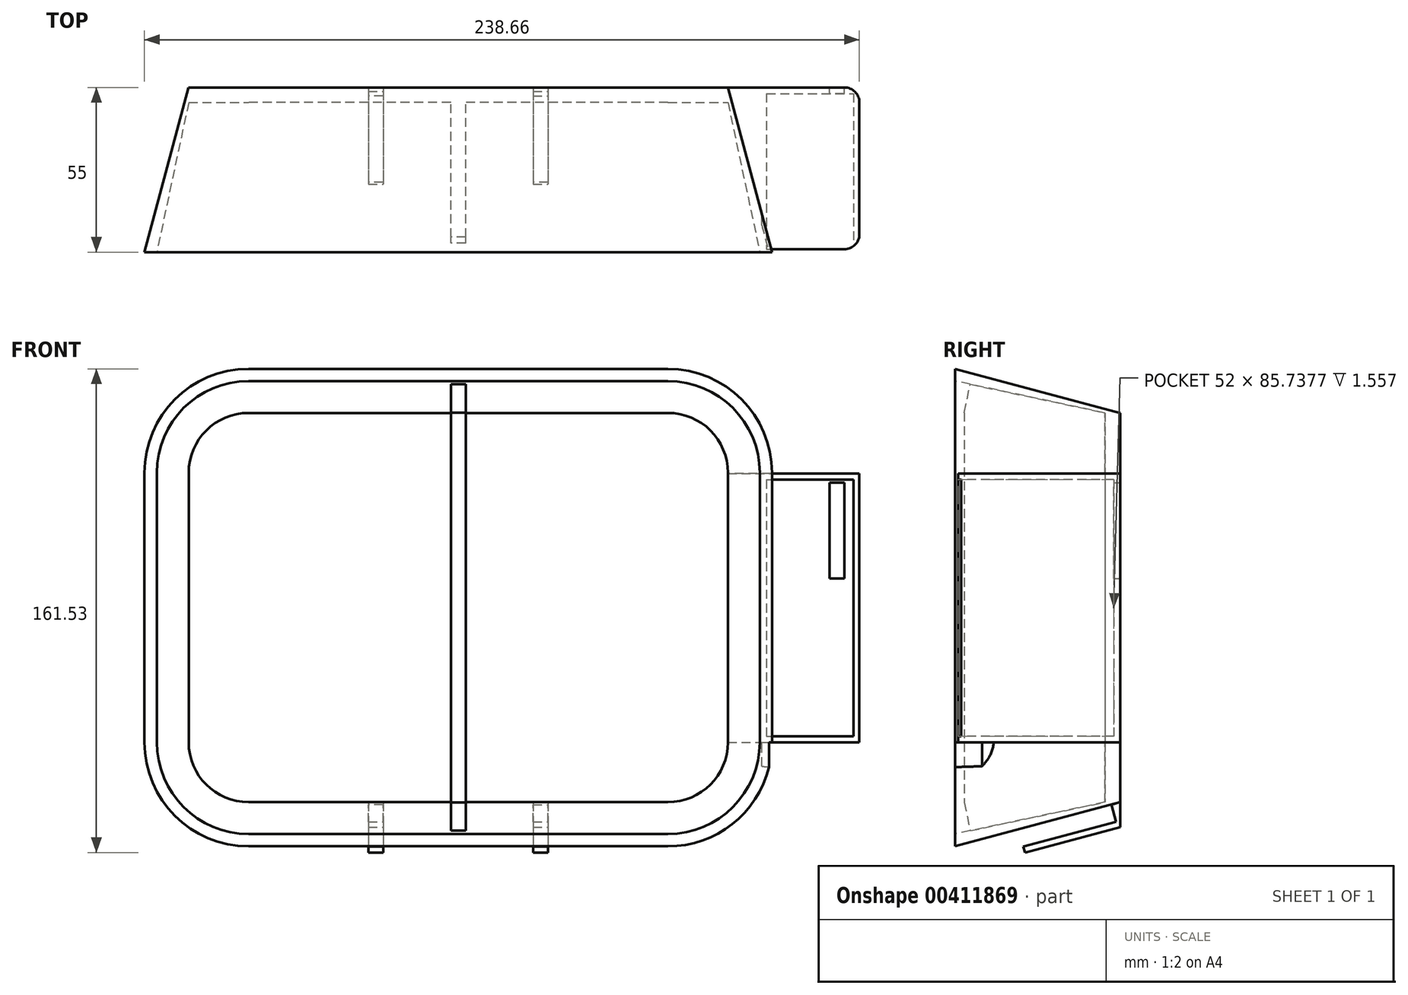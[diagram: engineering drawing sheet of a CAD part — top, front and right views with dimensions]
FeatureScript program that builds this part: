
annotation { "Feature Type Name" : "Feature", "Feature Type Description" : "" }
export const myFeature = defineFeature(function(context is Context, id is Id, definition is map)
    precondition{}
    {
        {
            var Q0;
            Q0=qCreatedBy(makeId("Front.planeOp"),FACE);
            var sketch = newSketch(context, id + "F0", { "sketchPlane" : qUnion([Q0])});
            skLineSegment(sketch, "E0.bottom", {"start": v(-105.92, 85.19) * mm, "end": v(34.08, 85.19) * mm});
            skLineSegment(sketch, "E0.top", {"start": v(-105.92, -44.81) * mm, "end": v(34.08, -44.81) * mm});
            skLineSegment(sketch, "E0.left", {"start": v(-125.92, 65.19) * mm, "end": v(-125.92, -24.81) * mm});
            skLineSegment(sketch, "E0.right", {"start": v(54.08, 65.19) * mm, "end": v(54.08, -24.81) * mm});
            skPoint(sketch, "E1.visualSharp", {"position": v(54.08, 85.19) * mm});
            skArc(sketch, "E1.filletArc", {"start": v(54.08, 65.19) * mm, "mid": v(48.22, 79.33) * mm, "end": v(34.08, 85.19) * mm});
            skArc(sketch, "E2.filletArc", {"start": v(34.08, -44.81) * mm, "mid": v(48.22, -38.95) * mm, "end": v(54.08, -24.81) * mm});
            skArc(sketch, "E3.filletArc", {"start": v(-125.92, -24.81) * mm, "mid": v(-120.06, -38.95) * mm, "end": v(-105.92, -44.81) * mm});
            skPoint(sketch, "E4.visualSharp", {"position": v(-125.92, 85.19) * mm});
            skArc(sketch, "E4.filletArc", {"start": v(-105.92, 85.19) * mm, "mid": v(-120.06, 79.33) * mm, "end": v(-125.92, 65.19) * mm});
            skSolve(sketch);
        }
        {
            var Q0;
            Q0=makeQuery(id+"F0.imprint","IMPRINT",FACE,{"disambiguationData":[TD([[makeQuery(id+"F0.imprint","IMPRINT",EDGE,{"derivedFrom":sQuery(id+"F0.wireOp",EDGE,"E0.bottom")}),-1.0]])]});
            extrude(context, id + "F1", {"entities" : qUnion([Q0]), "depth" : 55 * mm, "hasDraft" : true, "draftAngle" : 15 * degree});
        }
        {
            var Q0;
            Q0=makeQuery(id+"F1.opExtrude","CAP_FACE",FACE,{"disambiguationData":[OSD([sQuery(id+"F0.wireOp",EDGE,"E0.bottom"),sQuery(id+"F0.wireOp",EDGE,"E0.top"),sQuery(id+"F0.wireOp",EDGE,"E0.left"),sQuery(id+"F0.wireOp",EDGE,"E0.right"),sQuery(id+"F0.wireOp",EDGE,"E1.filletArc"),sQuery(id+"F0.wireOp",EDGE,"E2.filletArc"),sQuery(id+"F0.wireOp",EDGE,"E3.filletArc"),sQuery(id+"F0.wireOp",EDGE,"E4.filletArc")])],"isStart":false});
            cPlane(context, id + "F2", {"entities" : qUnion([Q0]), "cplaneType" : CPlaneType.OFFSET, "offset" : 50 * mm, "oppositeDirection" : true, "width" : 150 * mm, "height" : 150 * mm});
        }
        {
            var Q0;
            Q0=qCreatedBy(id+"F2.planeOp",FACE);
            var sketch = newSketch(context, id + "F3", { "sketchPlane" : qUnion([Q0])});
            skLineSegment(sketch, "E5.bottom", {"start": v(-105.9, 85.22) * mm, "end": v(34.1, 85.22) * mm});
            skLineSegment(sketch, "E5.top", {"start": v(-105.9, -44.78) * mm, "end": v(34.1, -44.78) * mm});
            skLineSegment(sketch, "E5.left", {"start": v(-125.9, 65.22) * mm, "end": v(-125.9, -24.78) * mm});
            skLineSegment(sketch, "E5.right", {"start": v(54.1, 65.22) * mm, "end": v(54.1, -24.78) * mm});
            skPoint(sketch, "E6.visualSharp", {"position": v(-125.9, 85.22) * mm});
            skArc(sketch, "E6.filletArc", {"start": v(-105.9, 85.22) * mm, "mid": v(-120.04, 79.36) * mm, "end": v(-125.9, 65.22) * mm});
            skPoint(sketch, "E7.visualSharp", {"position": v(-125.9, -44.78) * mm});
            skArc(sketch, "E7.filletArc", {"start": v(-125.9, -24.78) * mm, "mid": v(-120.04, -38.92) * mm, "end": v(-105.9, -44.78) * mm});
            skPoint(sketch, "E8.visualSharp", {"position": v(54.1, -44.78) * mm});
            skArc(sketch, "E8.filletArc", {"start": v(34.1, -44.78) * mm, "mid": v(48.25, -38.92) * mm, "end": v(54.1, -24.78) * mm});
            skPoint(sketch, "E9.visualSharp", {"position": v(54.1, 85.22) * mm});
            skArc(sketch, "E9.filletArc", {"start": v(54.1, 65.22) * mm, "mid": v(48.25, 79.36) * mm, "end": v(34.1, 85.22) * mm});
            skSolve(sketch);
        }
        {
            var Q0;
            Q0 = qSketchRegion(id + "F3", true);
            extrude(context, id + "F4", {"entities" : qUnion([Q0]), "operationType" : NewBodyOperationType.REMOVE, "depth" : 55 * mm, "hasDraft" : true, "draftAngle" : 12 * degree});
        }
        {
            var Q0;
            Q0=makeQuery(id+"F4.boolean.opBoolean","COPY",FACE,{"derivedFrom":makeQuery(id+"F4.opExtrude","CAP_FACE",FACE,{"disambiguationData":[OSD([sQuery(id+"F3.wireOp",EDGE,"E5.bottom"),sQuery(id+"F3.wireOp",EDGE,"E5.top"),sQuery(id+"F3.wireOp",EDGE,"E5.left"),sQuery(id+"F3.wireOp",EDGE,"E5.right"),sQuery(id+"F3.wireOp",EDGE,"E6.filletArc"),sQuery(id+"F3.wireOp",EDGE,"E7.filletArc"),sQuery(id+"F3.wireOp",EDGE,"E8.filletArc"),sQuery(id+"F3.wireOp",EDGE,"E9.filletArc")])],"isStart":true})});
            var sketch = newSketch(context, id + "F5", { "sketchPlane" : qUnion([Q0])});
            skLineSegment(sketch, "E10.bottom", {"start": v(-38.4, 85.22) * mm, "end": v(-33.4, 85.22) * mm});
            skLineSegment(sketch, "E10.top", {"start": v(-38.4, -64.78) * mm, "end": v(-33.4, -64.78) * mm});
            skLineSegment(sketch, "E10.left", {"start": v(-38.4, 85.22) * mm, "end": v(-38.4, -64.78) * mm});
            skLineSegment(sketch, "E10.right", {"start": v(-33.4, 85.22) * mm, "end": v(-33.4, -64.78) * mm});
            skSolve(sketch);
        }
        {
            var Q0;
            Q0=makeQuery(id+"F5.imprint","IMPRINT",FACE,{"disambiguationData":[TD([[makeQuery(id+"F5.imprint","IMPRINT",EDGE,{"derivedFrom":sQuery(id+"F5.wireOp",EDGE,"E10.bottom")}),-1.0]])]});
            extrude(context, id + "F6", {"entities" : qUnion([Q0]), "operationType" : NewBodyOperationType.ADD, "depth" : 47 * mm});
        }
        {
            var Q0;
            Q0=qCreatedBy(makeId("Right.planeOp"),FACE);
            cPlane(context, id + "F7", {"entities" : qUnion([Q0]), "cplaneType" : CPlaneType.OFFSET, "offset" : 98 * mm, "width" : 150 * mm, "height" : 150 * mm});
        }
        {
            var Q0;
            Q0=qCreatedBy(id+"F7.planeOp",FACE);
            var sketch = newSketch(context, id + "F8", { "sketchPlane" : qUnion([Q0])});
            skLineSegment(sketch, "E11.bottom", {"start": v(-54.03, 64.93) * mm, "end": v(0, 64.93) * mm});
            skLineSegment(sketch, "E11.top", {"start": v(-54.03, -25.17) * mm, "end": v(0, -25.17) * mm});
            skLineSegment(sketch, "E11.left", {"start": v(-54.03, 64.93) * mm, "end": v(-54.03, -25.17) * mm});
            skLineSegment(sketch, "E11.right", {"start": v(0, 64.93) * mm, "end": v(0, -25.17) * mm});
            skSolve(sketch);
        }
        {
            var Q0;
            Q0=makeQuery(id+"F1.opExtrude","SWEPT_FACE",FACE,{"disambiguationData":[OSD([sQuery(id+"F0.wireOp",EDGE,"E0.right")])]});
            var sketch = newSketch(context, id + "F9", { "sketchPlane" : qUnion([Q0])});
            skLineSegment(sketch, "E12.bottom", {"start": v(-69.94, 64.93) * mm, "end": v(-14, 64.93) * mm});
            skLineSegment(sketch, "E12.top", {"start": v(-69.94, -24.81) * mm, "end": v(-14, -24.81) * mm});
            skLineSegment(sketch, "E12.left", {"start": v(-69.94, 64.93) * mm, "end": v(-69.94, -24.81) * mm});
            skLineSegment(sketch, "E12.right", {"start": v(-14, 64.93) * mm, "end": v(-14, -24.81) * mm});
            skSolve(sketch);
        }
        {
            var Q0;
            Q0=qCreatedBy(makeId("Front.planeOp"),FACE);
            var sketch = newSketch(context, id + "F10", { "sketchPlane" : qUnion([Q0])});
            skLineSegment(sketch, "E13.bottom", {"start": v(185.4, 123.91) * mm, "end": v(-174.62, 123.91) * mm});
            skLineSegment(sketch, "E13.top", {"start": v(185.4, -101.96) * mm, "end": v(-174.62, -101.96) * mm});
            skLineSegment(sketch, "E13.left", {"start": v(185.4, 123.91) * mm, "end": v(185.4, -101.96) * mm});
            skLineSegment(sketch, "E13.right", {"start": v(-174.62, 123.91) * mm, "end": v(-174.62, -101.96) * mm});
            skSolve(sketch);
        }
        {
            var Q0;
            Q0 = qSketchRegion(id + "F10", true);
            extrude(context, id + "F11", {"entities" : qUnion([Q0]), "operationType" : NewBodyOperationType.REMOVE, "oppositeDirection" : true, "depth" : 25 * mm});
        }
        {
            var Q0;
            Q0=makeQuery(id+"F4.boolean.opBoolean","COPY",FACE,{"derivedFrom":makeQuery(id+"F4.opExtrude","SWEPT_FACE",FACE,{"disambiguationData":[OSD([sQuery(id+"F3.wireOp",EDGE,"E5.top")])]})});
            var sketch = newSketch(context, id + "F12", { "sketchPlane" : qUnion([Q0])});
            skLineSegment(sketch, "E14.bottom", {"start": v(-33.4, -60.2) * mm, "end": v(-38.4, -60.2) * mm});
            skLineSegment(sketch, "E14.top", {"start": v(-33.4, -14.2) * mm, "end": v(-38.4, -14.2) * mm});
            skLineSegment(sketch, "E14.left", {"start": v(-33.4, -60.2) * mm, "end": v(-33.4, -14.2) * mm});
            skLineSegment(sketch, "E14.right", {"start": v(-38.4, -60.2) * mm, "end": v(-38.4, -14.2) * mm});
            skSolve(sketch);
        }
        {
            var Q0;
            Q0 = qSketchRegion(id + "F12", true);
            extrude(context, id + "F13", {"entities" : qUnion([Q0]), "operationType" : NewBodyOperationType.ADD, "depth" : 15 * mm});
        }
        {
            var Q0;
            Q0=makeQuery(id+"F4.boolean.opBoolean","COPY",FACE,{"derivedFrom":makeQuery(id+"F4.opExtrude","SWEPT_FACE",FACE,{"disambiguationData":[OSD([sQuery(id+"F3.wireOp",EDGE,"E5.bottom")])]})});
            var sketch = newSketch(context, id + "F14", { "sketchPlane" : qUnion([Q0])});
            skLineSegment(sketch, "E15.bottom", {"start": v(-38.4, 68.6) * mm, "end": v(-33.4, 68.6) * mm});
            skLineSegment(sketch, "E15.top", {"start": v(-38.4, 22.6) * mm, "end": v(-33.4, 22.6) * mm});
            skLineSegment(sketch, "E15.left", {"start": v(-38.4, 68.6) * mm, "end": v(-38.4, 22.6) * mm});
            skLineSegment(sketch, "E15.right", {"start": v(-33.4, 68.6) * mm, "end": v(-33.4, 22.6) * mm});
            skSolve(sketch);
        }
        {
            var Q0;
            Q0=makeQuery(id+"F14.imprint","IMPRINT",FACE,{"disambiguationData":[TD([[makeQuery(id+"F14.imprint","IMPRINT",EDGE,{"derivedFrom":sQuery(id+"F14.wireOp",EDGE,"E15.bottom")}),-1.0]])]});
            extrude(context, id + "F15", {"entities" : qUnion([Q0]), "operationType" : NewBodyOperationType.ADD, "depth" : 15 * mm});
        }
        {
            var Q0;
            Q0=makeQuery(id+"F8.imprint","IMPRINT",FACE,{"disambiguationData":[TD([[makeQuery(id+"F8.imprint","IMPRINT",EDGE,{"derivedFrom":sQuery(id+"F8.wireOp",EDGE,"E11.bottom")}),-1.0]])]});
            extrude(context, id + "F16", {"entities" : qUnion([Q0]), "operationType" : NewBodyOperationType.ADD, "oppositeDirection" : true, "depth" : 32.6 * mm});
        }
        {
            var Q0;
            Q0=makeQuery(id+"F9.imprint","IMPRINT",FACE,{"disambiguationData":[TD([[makeQuery(id+"F9.imprint","IMPRINT",EDGE,{"derivedFrom":sQuery(id+"F9.wireOp",EDGE,"E12.bottom")}),-1.0]])]});
            extrude(context, id + "F17", {"entities" : qUnion([Q0]), "operationType" : NewBodyOperationType.ADD, "depth" : 25 * mm});
        }
        {
            var Q0;
            Q0=qCreatedBy(makeId("Front.planeOp"),FACE);
            var sketch = newSketch(context, id + "F18", { "sketchPlane" : qUnion([Q0])});
            skLineSegment(sketch, "E16.bottom", {"start": v(-173.75, 128.8) * mm, "end": v(173.98, 128.8) * mm});
            skLineSegment(sketch, "E16.top", {"start": v(-173.75, -88.43) * mm, "end": v(173.98, -88.43) * mm});
            skLineSegment(sketch, "E16.left", {"start": v(-173.75, 128.8) * mm, "end": v(-173.75, -88.43) * mm});
            skLineSegment(sketch, "E16.right", {"start": v(173.98, 128.8) * mm, "end": v(173.98, -88.43) * mm});
            skSolve(sketch);
        }
        {
            var Q0;
            Q0 = qSketchRegion(id + "F18", true);
            extrude(context, id + "F19", {"entities" : qUnion([Q0]), "operationType" : NewBodyOperationType.REMOVE, "oppositeDirection" : true, "depth" : 25 * mm});
        }
        {
            var Q0;
            Q0=makeQuery(id+"F17.opExtrude","SWEPT_FACE",FACE,{"disambiguationData":[OSD([sQuery(id+"F9.wireOp",EDGE,"E12.top")])]});
            var sketch = newSketch(context, id + "F20", { "sketchPlane" : qUnion([Q0])});
            skLineSegment(sketch, "E17.bottom", {"start": v(65.4, 45.99) * mm, "end": v(99.8, 45.99) * mm});
            skLineSegment(sketch, "E17.top", {"start": v(65.4, 0) * mm, "end": v(99.8, 0) * mm});
            skLineSegment(sketch, "E17.left", {"start": v(65.4, 45.99) * mm, "end": v(65.4, 0) * mm});
            skLineSegment(sketch, "E17.right", {"start": v(99.8, 45.99) * mm, "end": v(99.8, 0) * mm});
            skPoint(sketch, "E18.end.orphan", {"position": v(97.92, 45.99) * mm});
            skLineSegment(sketch, "E19", {"start": v(65.4, 45.99) * mm, "end": v(68.02, 55.75) * mm});
            skLineSegment(sketch, "E20", {"start": v(68.02, 55.75) * mm, "end": v(100.28, 55.75) * mm});
            skLineSegment(sketch, "E21", {"start": v(100.28, 55.75) * mm, "end": v(99.8, 45.99) * mm});
            skSolve(sketch);
        }
        {
            var Q0;
            Q0 = qSketchRegion(id + "F20", true);
            extrude(context, id + "F21", {"entities" : qUnion([Q0]), "operationType" : NewBodyOperationType.REMOVE, "depth" : 25 * mm});
        }
        {
            var Q0;
            {var subQ0=sQuery(id+"F8.wireOp",EDGE,"E11.left");var subQ1=sQuery(id+"F8.wireOp",EDGE,"E11.bottom");var subQ3=makeQuery(id+"F16.opExtrude","SWEPT_FACE",FACE,{"disambiguationData":[OSD([subQ0])]});Q0=makeQuery(id+"F21.boolean.opBoolean","SPLIT",FACE,{"disambiguationData":[TD([makeQuery(id+"F16.opExtrude","SWEPT_FACE",FACE,{"disambiguationData":[OSD([subQ1])]})])],"derivedFrom":subQ3});}
            var sketch = newSketch(context, id + "F22", { "sketchPlane" : qUnion([Q0])});
            skLineSegment(sketch, "E22.bottom", {"start": v(67, 62.93) * mm, "end": v(96, 62.93) * mm});
            skLineSegment(sketch, "E22.top", {"start": v(67, -22.81) * mm, "end": v(96, -22.81) * mm});
            skLineSegment(sketch, "E22.left", {"start": v(67, 62.93) * mm, "end": v(67, -22.81) * mm});
            skLineSegment(sketch, "E22.right", {"start": v(96, 62.93) * mm, "end": v(96, -22.81) * mm});
            skSolve(sketch);
        }
        {
            var Q0;
            Q0=makeQuery(id+"F22.imprint","IMPRINT",FACE,{"disambiguationData":[TD([[makeQuery(id+"F22.imprint","IMPRINT",EDGE,{"derivedFrom":sQuery(id+"F22.wireOp",EDGE,"E22.bottom")}),-1.0]])]});
            extrude(context, id + "F23", {"entities" : qUnion([Q0]), "operationType" : NewBodyOperationType.REMOVE, "oppositeDirection" : true, "depth" : 52 * mm});
        }
        {
            var Q0;
            Q0=makeQuery(id+"F16.opExtrude","CAP_EDGE",EDGE,{"disambiguationData":[OSD([sQuery(id+"F8.wireOp",EDGE,"E11.left")])],"isStart":true});
            var Q1;
            Q1=makeQuery(id+"F16.opExtrude","CAP_EDGE",EDGE,{"disambiguationData":[OSD([sQuery(id+"F8.wireOp",EDGE,"E11.right")])],"isStart":true});
            fillet(context, id + "F24", {"entities" : qUnion([Q0, Q1]), "radius" : 5 * mm, "tangentPropagation" : true, "allowEdgeOverflow" : false});
        }
        {
            var Q0;
            Q0=makeQuery(id+"F6.opExtrude","CAP_FACE",FACE,{"disambiguationData":[OSD([sQuery(id+"F3.wireOp",EDGE,"E5.top"),sQuery(id+"F5.wireOp",EDGE,"E10.bottom"),sQuery(id+"F5.wireOp",EDGE,"E10.left"),sQuery(id+"F5.wireOp",EDGE,"E10.right")])],"isStart":false});
            var sketch = newSketch(context, id + "F25", { "sketchPlane" : qUnion([Q0])});
            skLineSegment(sketch, "E23.bottom", {"start": v(-38.4, 92.26) * mm, "end": v(-33.4, 92.26) * mm});
            skLineSegment(sketch, "E23.top", {"start": v(-38.4, -53.07) * mm, "end": v(-33.4, -53.07) * mm});
            skLineSegment(sketch, "E23.left", {"start": v(-38.4, 92.26) * mm, "end": v(-38.4, -56.27) * mm});
            skLineSegment(sketch, "E23.right", {"start": v(-33.4, 92.26) * mm, "end": v(-33.4, -56.27) * mm});
            skSolve(sketch);
        }
        {
            var Q0;
            Q0 = qSketchRegion(id + "F25", true);
            extrude(context, id + "F26", {"entities" : qUnion([Q0]), "operationType" : NewBodyOperationType.REMOVE, "depth" : 25 * mm});
        }
        {
            var Q0;
            Q0=makeQuery(id+"F19.boolean.opBoolean","MERGE",FACE,{"derivedFrom":[makeQuery(id+"F1.opExtrude","CAP_FACE",FACE,{"disambiguationData":[OSD([sQuery(id+"F0.wireOp",EDGE,"E0.bottom"),sQuery(id+"F0.wireOp",EDGE,"E0.top"),sQuery(id+"F0.wireOp",EDGE,"E0.left"),sQuery(id+"F0.wireOp",EDGE,"E0.right"),sQuery(id+"F0.wireOp",EDGE,"E1.filletArc"),sQuery(id+"F0.wireOp",EDGE,"E2.filletArc"),sQuery(id+"F0.wireOp",EDGE,"E3.filletArc"),sQuery(id+"F0.wireOp",EDGE,"E4.filletArc")])],"isStart":true}),makeQuery(id+"F16.opExtrude","SWEPT_FACE",FACE,{"disambiguationData":[OSD([sQuery(id+"F8.wireOp",EDGE,"E11.right")])]}),makeQuery(id+"F19.opExtrude","CAP_FACE",FACE,{"disambiguationData":[OSD([sQuery(id+"F18.wireOp",EDGE,"E16.bottom"),sQuery(id+"F18.wireOp",EDGE,"E16.top"),sQuery(id+"F18.wireOp",EDGE,"E16.left"),sQuery(id+"F18.wireOp",EDGE,"E16.right")])],"isStart":true})]});
            var sketch = newSketch(context, id + "F27", { "sketchPlane" : qUnion([Q0])});
            skLineSegment(sketch, "E24.bottom", {"start": v(-88, 29.93) * mm, "end": v(-93, 29.93) * mm});
            skLineSegment(sketch, "E24.top", {"start": v(-88, 61.93) * mm, "end": v(-93, 61.93) * mm});
            skLineSegment(sketch, "E24.left", {"start": v(-88, 29.93) * mm, "end": v(-88, 61.93) * mm});
            skLineSegment(sketch, "E24.right", {"start": v(-93, 29.93) * mm, "end": v(-93, 61.93) * mm});
            skSolve(sketch);
        }
        {
            var Q0;
            Q0 = qSketchRegion(id + "F27", true);
            extrude(context, id + "F28", {"entities" : qUnion([Q0]), "operationType" : NewBodyOperationType.REMOVE, "oppositeDirection" : true, "depth" : 10 * mm});
        }
        {
            var Q0;
            Q0=makeQuery(id+"F1.opExtrude","SWEPT_FACE",FACE,{"disambiguationData":[OSD([sQuery(id+"F0.wireOp",EDGE,"E0.top")])]});
            var sketch = newSketch(context, id + "F29", { "sketchPlane" : qUnion([Q0])});
            skLineSegment(sketch, "E25.bottom", {"start": v(-60.92, 11.6) * mm, "end": v(-65.92, 11.6) * mm});
            skLineSegment(sketch, "E25.top", {"start": v(-60.92, 46.6) * mm, "end": v(-65.92, 46.6) * mm});
            skLineSegment(sketch, "E25.left", {"start": v(-60.92, 11.6) * mm, "end": v(-60.92, 46.6) * mm});
            skLineSegment(sketch, "E25.right", {"start": v(-65.92, 11.6) * mm, "end": v(-65.92, 46.6) * mm});
            skLineSegment(sketch, "E26.bottom", {"start": v(-5.92, 11.6) * mm, "end": v(-10.92, 11.6) * mm});
            skLineSegment(sketch, "E26.top", {"start": v(-5.92, 46.6) * mm, "end": v(-10.92, 46.6) * mm});
            skLineSegment(sketch, "E26.left", {"start": v(-5.92, 11.6) * mm, "end": v(-5.92, 46.6) * mm});
            skLineSegment(sketch, "E26.right", {"start": v(-10.92, 11.6) * mm, "end": v(-10.92, 46.6) * mm});
            skSolve(sketch);
        }
        {
            var Q0;
            Q0=makeQuery(id+"F29.imprint","IMPRINT",FACE,{"disambiguationData":[TD([[makeQuery(id+"F29.imprint","IMPRINT",EDGE,{"derivedFrom":sQuery(id+"F29.wireOp",EDGE,"E25.bottom")}),1.0]])]});
            var Q1;
            Q1=makeQuery(id+"F29.imprint","IMPRINT",FACE,{"disambiguationData":[TD([[makeQuery(id+"F29.imprint","IMPRINT",EDGE,{"derivedFrom":sQuery(id+"F29.wireOp",EDGE,"E26.bottom")}),1.0]])]});
            extrude(context, id + "F30", {"entities" : qUnion([Q0, Q1]), "operationType" : NewBodyOperationType.ADD, "depth" : 8 * mm});
        }
        {
            var Q0;
            Q0=makeQuery(id+"F19.boolean.opBoolean","MERGE",FACE,{"derivedFrom":[makeQuery(id+"F1.opExtrude","CAP_FACE",FACE,{"disambiguationData":[OSD([sQuery(id+"F0.wireOp",EDGE,"E0.bottom"),sQuery(id+"F0.wireOp",EDGE,"E0.top"),sQuery(id+"F0.wireOp",EDGE,"E0.left"),sQuery(id+"F0.wireOp",EDGE,"E0.right"),sQuery(id+"F0.wireOp",EDGE,"E1.filletArc"),sQuery(id+"F0.wireOp",EDGE,"E2.filletArc"),sQuery(id+"F0.wireOp",EDGE,"E3.filletArc"),sQuery(id+"F0.wireOp",EDGE,"E4.filletArc")])],"isStart":true}),makeQuery(id+"F16.opExtrude","SWEPT_FACE",FACE,{"disambiguationData":[OSD([sQuery(id+"F8.wireOp",EDGE,"E11.right")])]}),makeQuery(id+"F19.opExtrude","CAP_FACE",FACE,{"disambiguationData":[OSD([sQuery(id+"F18.wireOp",EDGE,"E16.bottom"),sQuery(id+"F18.wireOp",EDGE,"E16.top"),sQuery(id+"F18.wireOp",EDGE,"E16.left"),sQuery(id+"F18.wireOp",EDGE,"E16.right")])],"isStart":true})]});
            var sketch = newSketch(context, id + "F31", { "sketchPlane" : qUnion([Q0])});
            skLineSegment(sketch, "E27.bottom", {"start": v(-29.21, -24.26) * mm, "end": v(93.32, -24.26) * mm});
            skLineSegment(sketch, "E27.top", {"start": v(-29.21, -73.08) * mm, "end": v(93.32, -73.08) * mm});
            skLineSegment(sketch, "E27.left", {"start": v(-29.21, -24.26) * mm, "end": v(-29.21, -73.08) * mm});
            skLineSegment(sketch, "E27.right", {"start": v(93.32, -24.26) * mm, "end": v(93.32, -73.08) * mm});
            skSolve(sketch);
        }
        {
            var Q0;
            Q0 = qSketchRegion(id + "F31", true);
            extrude(context, id + "F32", {"entities" : qUnion([Q0]), "operationType" : NewBodyOperationType.REMOVE, "depth" : 25 * mm});
        }
        {
            var Q0;
            Q0=makeQuery(id+"F30.opExtrude","SWEPT_FACE",FACE,{"disambiguationData":[OSD([sQuery(id+"F29.wireOp",EDGE,"E25.top")])]});
            var sketch = newSketch(context, id + "F33", { "sketchPlane" : qUnion([Q0])});
            skLineSegment(sketch, "E28.bottom", {"start": v(-65.92, -43.28) * mm, "end": v(-60.92, -43.28) * mm});
            skLineSegment(sketch, "E28.top", {"start": v(-65.92, -49.28) * mm, "end": v(-60.92, -49.28) * mm});
            skLineSegment(sketch, "E28.left", {"start": v(-65.92, -43.28) * mm, "end": v(-65.92, -49.28) * mm});
            skLineSegment(sketch, "E28.right", {"start": v(-60.92, -43.28) * mm, "end": v(-60.92, -49.28) * mm});
            skLineSegment(sketch, "E29.bottom", {"start": v(-11.78, -43.28) * mm, "end": v(-5.78, -43.28) * mm});
            skLineSegment(sketch, "E29.top", {"start": v(-11.78, -49.28) * mm, "end": v(-5.78, -49.28) * mm});
            skLineSegment(sketch, "E29.left", {"start": v(-11.78, -43.28) * mm, "end": v(-11.78, -49.28) * mm});
            skLineSegment(sketch, "E29.right", {"start": v(-5.78, -43.28) * mm, "end": v(-5.78, -49.28) * mm});
            skSolve(sketch);
        }
        {
            var Q0;
            Q0 = qSketchRegion(id + "F33", true);
            extrude(context, id + "F34", {"entities" : qUnion([Q0]), "operationType" : NewBodyOperationType.REMOVE, "oppositeDirection" : true, "depth" : 32 * mm});
        }
    });
